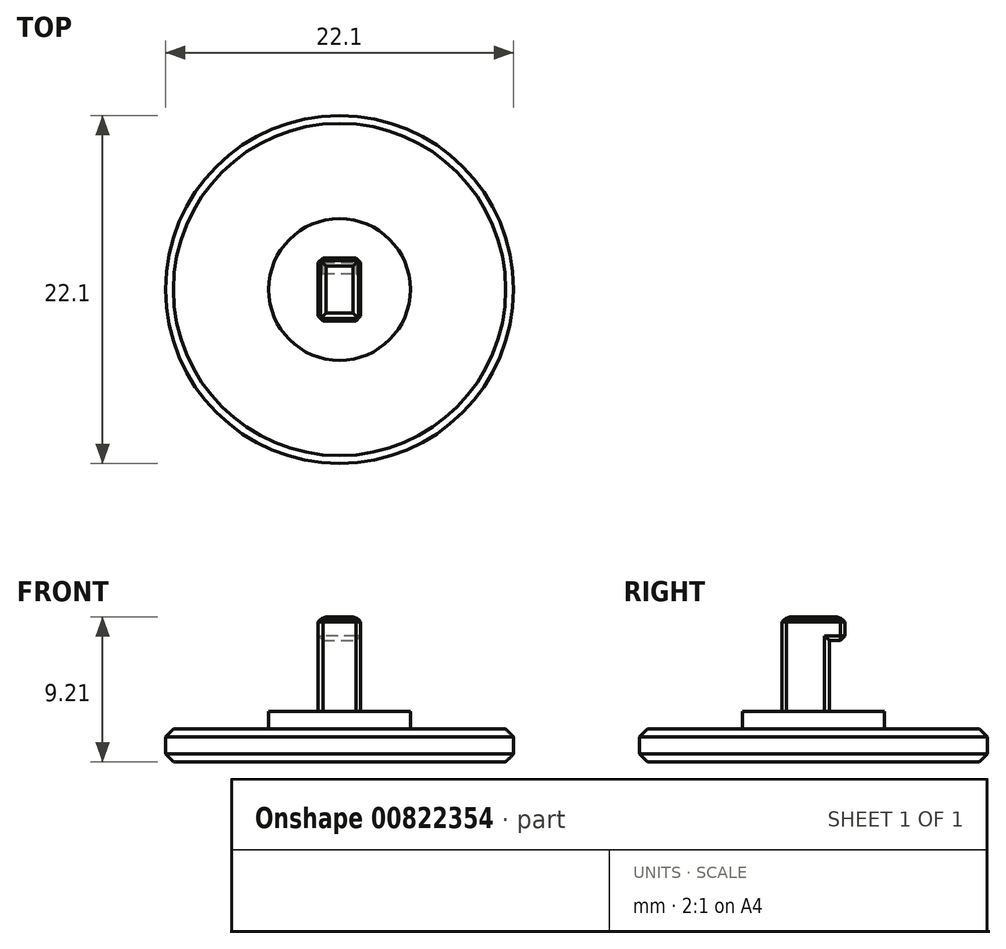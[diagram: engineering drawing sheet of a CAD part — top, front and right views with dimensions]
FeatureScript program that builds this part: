
annotation { "Feature Type Name" : "Feature", "Feature Type Description" : "" }
export const myFeature = defineFeature(function(context is Context, id is Id, definition is map)
    precondition{}
    {
        {
            var Q0;
            Q0=qCreatedBy(makeId("Top.planeOp"),FACE);
            var sketch = newSketch(context, id + "F0", { "sketchPlane" : qUnion([Q0])});
            skCircle(sketch, "E0", {"center": v(0, 0) * mm, "radius": 11.05 * mm});
            skSolve(sketch);
        }
        {
            var Q0;
            Q0=qSketchRegion(id+"F0",true);
            extrude(context, id + "F1", {"entities" : qUnion([Q0]), "depth" : 2.1 * mm, "offsetDistance" : 25 * mm});
        }
        {
            var Q0;
            Q0=makeQuery(id+"F1.opExtrude","CAP_FACE",FACE,{"disambiguationData":[OSD([sQuery(id+"F0.wireOp",EDGE,"E0")])],"isStart":false});
            var sketch = newSketch(context, id + "F2", { "sketchPlane" : qUnion([Q0])});
            skCircle(sketch, "E1", {"center": v(0, 0) * mm, "radius": 4.5 * mm});
            skSolve(sketch);
        }
        {
            var Q0;
            Q0=makeQuery(id+"F2.imprint","IMPRINT",FACE,{"disambiguationData":[TD([[makeQuery(id+"F2.imprint","IMPRINT",EDGE,{"derivedFrom":sQuery(id+"F2.wireOp",EDGE,"E1")}),1.0]])]});
            extrude(context, id + "F3", {"entities" : qUnion([Q0]), "operationType" : NewBodyOperationType.ADD, "depth" : 1.11 * mm, "offsetDistance" : 25 * mm});
        }
        {
            var Q0;
            Q0=makeQuery(id+"F3.opExtrude","CAP_FACE",FACE,{"disambiguationData":[OSD([sQuery(id+"F2.wireOp",EDGE,"E1")])],"isStart":false});
            var sketch = newSketch(context, id + "F4", { "sketchPlane" : qUnion([Q0])});
            skCircle(sketch, "E2", {"center": v(0, 0) * mm, "radius": 4 * mm});
            skSolve(sketch);
        }
        {
            var Q0;
            Q0=makeQuery(id+"F4.imprint","IMPRINT",FACE,{"disambiguationData":[TD([[makeQuery(id+"F4.imprint","IMPRINT",EDGE,{"derivedFrom":sQuery(id+"F4.wireOp",EDGE,"E2")}),1.0]])]});
            var sketch = newSketch(context, id + "F5", { "sketchPlane" : qUnion([Q0])});
            skLineSegment(sketch, "E3.top", {"start": v(1.35, -2) * mm, "end": v(-1.35, -2) * mm});
            skLineSegment(sketch, "E3.left", {"start": v(1.35, 1) * mm, "end": v(1.35, -2) * mm});
            skLineSegment(sketch, "E3.right", {"start": v(-1.35, 1) * mm, "end": v(-1.35, -2) * mm});
            skPoint(sketch, "E3.middle", {"position": v(0, 0) * mm});
            skLineSegment(sketch, "E4.bottom", {"start": v(-1.35, -2) * mm, "end": v(1.35, -2) * mm});
            skLineSegment(sketch, "E4.left", {"start": v(-1.35, -2) * mm, "end": v(-1.35, 0) * mm});
            skLineSegment(sketch, "E4.right", {"start": v(1.35, -2) * mm, "end": v(1.35, 0) * mm});
            skLineSegment(sketch, "E5.top", {"start": v(-1.35, 1) * mm, "end": v(1.35, 1) * mm});
            skLineSegment(sketch, "E5.left", {"start": v(-1.35, 0) * mm, "end": v(-1.35, 1) * mm});
            skLineSegment(sketch, "E5.right", {"start": v(1.35, 0) * mm, "end": v(1.35, 1) * mm});
            skPoint(sketch, "E6.orphan", {"position": v(-1.35, 2) * mm});
            skPoint(sketch, "E7.orphan", {"position": v(1.35, 2) * mm});
            skSolve(sketch);
        }
        {
            var Q0;
            {var subQ1=sQuery(id+"F5.wireOp",EDGE,"E3.top");Q0=makeQuery(id+"F5.imprint","IMPRINT",FACE,{"disambiguationData":[TD([[makeQuery(id+"F5.imprint","IMPRINT",EDGE,{"derivedFrom":subQ1}),-1.0]])]});}
            extrude(context, id + "F6", {"entities" : qUnion([Q0]), "operationType" : NewBodyOperationType.ADD, "depth" : 6 * mm, "offsetDistance" : 25 * mm});
        }
        {
            var Q0;
            Q0=makeQuery(id+"F6.opExtrude","SWEPT_FACE",FACE,{"disambiguationData":[OSD([sQuery(id+"F5.wireOp",EDGE,"E5.top")])]});
            var sketch = newSketch(context, id + "F7", { "sketchPlane" : qUnion([Q0])});
            skLineSegment(sketch, "E8.bottom", {"start": v(1.35, 9.2) * mm, "end": v(-1.35, 9.2) * mm});
            skLineSegment(sketch, "E8.top", {"start": v(1.35, 7.7) * mm, "end": v(-1.35, 7.7) * mm});
            skLineSegment(sketch, "E8.left", {"start": v(1.35, 9.2) * mm, "end": v(1.35, 7.7) * mm});
            skLineSegment(sketch, "E8.right", {"start": v(-1.35, 9.2) * mm, "end": v(-1.35, 7.7) * mm});
            skSolve(sketch);
        }
        {
            var Q0;
            Q0=makeQuery(id+"F7.imprint","IMPRINT",FACE,{"disambiguationData":[TD([[makeQuery(id+"F7.imprint","IMPRINT",EDGE,{"derivedFrom":sQuery(id+"F7.wireOp",EDGE,"E8.bottom")}),1.0]])]});
            extrude(context, id + "F8", {"entities" : qUnion([Q0]), "operationType" : NewBodyOperationType.ADD, "depth" : 1 * mm, "offsetDistance" : 25 * mm});
        }
        {
            var Q0;
            Q0=makeQuery(id+"F6.opExtrude","SWEPT_EDGE",EDGE,{"disambiguationData":[OSD([sQuery(id+"F5.wireOp",EDGE,"E3.top"),sQuery(id+"F5.wireOp",EDGE,"E3.right")])]});
            var Q1;
            Q1=makeQuery(id+"F6.opExtrude","SWEPT_EDGE",EDGE,{"disambiguationData":[OSD([sQuery(id+"F5.wireOp",EDGE,"E3.top"),sQuery(id+"F5.wireOp",EDGE,"E3.left")])]});
            var Q2;
            Q2=makeQuery(id+"F6.opExtrude","SWEPT_EDGE",EDGE,{"disambiguationData":[OSD([sQuery(id+"F5.wireOp",EDGE,"E3.left"),sQuery(id+"F5.wireOp",EDGE,"E5.top")])]});
            var Q3;
            Q3=makeQuery(id+"F6.opExtrude","SWEPT_EDGE",EDGE,{"disambiguationData":[OSD([sQuery(id+"F5.wireOp",EDGE,"E3.right"),sQuery(id+"F5.wireOp",EDGE,"E5.top")])]});
            var Q4;
            Q4=makeQuery(id+"F8.opExtrude","SWEPT_EDGE",EDGE,{"disambiguationData":[OSD([sQuery(id+"F5.wireOp",EDGE,"E3.left"),sQuery(id+"F5.wireOp",EDGE,"E5.top"),sQuery(id+"F7.wireOp",EDGE,"E8.top"),sQuery(id+"F7.wireOp",EDGE,"E8.right")])]});
            var Q5;
            Q5=makeQuery(id+"F8.opExtrude","SWEPT_EDGE",EDGE,{"disambiguationData":[OSD([sQuery(id+"F5.wireOp",EDGE,"E3.right"),sQuery(id+"F5.wireOp",EDGE,"E5.top"),sQuery(id+"F7.wireOp",EDGE,"E8.top"),sQuery(id+"F7.wireOp",EDGE,"E8.left")])]});
            var Q6;
            Q6=makeQuery(id+"F8.opExtrude","CAP_EDGE",EDGE,{"disambiguationData":[OSD([sQuery(id+"F7.wireOp",EDGE,"E8.top")])],"isStart":false});
            var Q7;
            Q7=makeQuery(id+"F8.opExtrude","CAP_EDGE",EDGE,{"disambiguationData":[OSD([sQuery(id+"F7.wireOp",EDGE,"E8.right")])],"isStart":false});
            var Q8;
            Q8=makeQuery(id+"F8.opExtrude","CAP_EDGE",EDGE,{"disambiguationData":[OSD([sQuery(id+"F7.wireOp",EDGE,"E8.left")])],"isStart":false});
            var Q9;
            Q9=makeQuery(id+"F8.opExtrude","CAP_EDGE",EDGE,{"disambiguationData":[OSD([sQuery(id+"F7.wireOp",EDGE,"E8.bottom")])],"isStart":false});
            var Q10;
            Q10=makeQuery(id+"F8.boolean.opBoolean","MERGE",EDGE,{"derivedFrom":[makeQuery(id+"F6.opExtrude","CAP_EDGE",EDGE,{"disambiguationData":[OSD([sQuery(id+"F5.wireOp",EDGE,"E3.left")])],"isStart":false}),makeQuery(id+"F8.opExtrude","SWEPT_EDGE",EDGE,{"disambiguationData":[OSD([sQuery(id+"F7.wireOp",EDGE,"E8.bottom"),sQuery(id+"F7.wireOp",EDGE,"E8.right")])]})]});
            var Q11;
            Q11=makeQuery(id+"F8.boolean.opBoolean","MERGE",EDGE,{"derivedFrom":[makeQuery(id+"F6.opExtrude","CAP_EDGE",EDGE,{"disambiguationData":[OSD([sQuery(id+"F5.wireOp",EDGE,"E3.right")])],"isStart":false}),makeQuery(id+"F8.opExtrude","SWEPT_EDGE",EDGE,{"disambiguationData":[OSD([sQuery(id+"F7.wireOp",EDGE,"E8.bottom"),sQuery(id+"F7.wireOp",EDGE,"E8.left")])]})]});
            var Q12;
            Q12=makeQuery(id+"F6.opExtrude","CAP_EDGE",EDGE,{"disambiguationData":[OSD([sQuery(id+"F5.wireOp",EDGE,"E3.top")])],"isStart":false});
            var Q13;
            Q13=makeQuery(id+"F6.opExtrude","CAP_EDGE",EDGE,{"disambiguationData":[OSD([sQuery(id+"F5.wireOp",EDGE,"E3.right")])],"isStart":true});
            chamfer(context, id + "F9", {"entities" : qUnion([Q0, Q1, Q2, Q3, Q4, Q5, Q6, Q7, Q8, Q9, Q10, Q11, Q12, Q13]), "width" : .3 * mm, "tangentPropagation" : true});
        }
        {
            var Q0;
            Q0=makeQuery(id+"F1.opExtrude","CAP_EDGE",EDGE,{"disambiguationData":[OSD([sQuery(id+"F0.wireOp",EDGE,"E0")])],"isStart":true});
            var Q1;
            Q1=makeQuery(id+"F1.opExtrude","CAP_EDGE",EDGE,{"disambiguationData":[OSD([sQuery(id+"F0.wireOp",EDGE,"E0")])],"isStart":false});
            chamfer(context, id + "F10", {"entities" : qUnion([Q0, Q1]), "width" : .5 * mm, "tangentPropagation" : true});
        }
        {
            var Q0;
            Q0=makeQuery(id+"F6.opExtrude","SWEPT_EDGE",EDGE,{"disambiguationData":[OSD([sQuery(id+"F5.wireOp",EDGE,"E4.bottom"),sQuery(id+"F5.wireOp",EDGE,"E4.right")])]});
            var Q1;
            Q1=makeQuery(id+"F6.opExtrude","SWEPT_EDGE",EDGE,{"disambiguationData":[OSD([sQuery(id+"F5.wireOp",EDGE,"E5.top"),sQuery(id+"F5.wireOp",EDGE,"E5.right")])]});
            var Q2;
            Q2=makeQuery(id+"F6.opExtrude","SWEPT_EDGE",EDGE,{"disambiguationData":[OSD([sQuery(id+"F5.wireOp",EDGE,"E5.top"),sQuery(id+"F5.wireOp",EDGE,"E5.left")])]});
            var Q3;
            Q3=makeQuery(id+"F8.opExtrude","CAP_EDGE",EDGE,{"disambiguationData":[OSD([sQuery(id+"F7.wireOp",EDGE,"E8.top")])],"isStart":true});
            var Q4;
            Q4=makeQuery(id+"F8.opExtrude","CAP_EDGE",EDGE,{"disambiguationData":[OSD([sQuery(id+"F7.wireOp",EDGE,"E8.right")])],"isStart":false});
            var Q5;
            Q5=makeQuery(id+"F8.boolean.opBoolean","MERGE",FACE,{"derivedFrom":[makeQuery(id+"F6.opExtrude","CAP_FACE",FACE,{"disambiguationData":[OSD([sQuery(id+"F5.wireOp",EDGE,"E3.top"),sQuery(id+"F5.wireOp",EDGE,"E3.left"),sQuery(id+"F5.wireOp",EDGE,"E3.right"),sQuery(id+"F5.wireOp",EDGE,"E5.top")])],"isStart":false}),makeQuery(id+"F8.opExtrude","SWEPT_FACE",FACE,{"disambiguationData":[OSD([sQuery(id+"F7.wireOp",EDGE,"E8.bottom")])]})]});
            var Q6;
            Q6=makeQuery(id+"F6.opExtrude","SWEPT_EDGE",EDGE,{"disambiguationData":[OSD([sQuery(id+"F5.wireOp",EDGE,"E4.bottom"),sQuery(id+"F5.wireOp",EDGE,"E4.left")])]});
            var Q7;
            Q7=makeQuery(id+"F8.opExtrude","SWEPT_EDGE",EDGE,{"disambiguationData":[OSD([sQuery(id+"F5.wireOp",EDGE,"E5.top"),sQuery(id+"F5.wireOp",EDGE,"E5.left"),sQuery(id+"F7.wireOp",EDGE,"E8.top"),sQuery(id+"F7.wireOp",EDGE,"E8.left")])]});
            var Q8;
            Q8=makeQuery(id+"F8.opExtrude","CAP_EDGE",EDGE,{"disambiguationData":[OSD([sQuery(id+"F7.wireOp",EDGE,"E8.left")])],"isStart":false});
            var Q9;
            Q9=makeQuery(id+"F8.opExtrude","SWEPT_EDGE",EDGE,{"disambiguationData":[OSD([sQuery(id+"F5.wireOp",EDGE,"E5.top"),sQuery(id+"F5.wireOp",EDGE,"E5.right"),sQuery(id+"F7.wireOp",EDGE,"E8.top"),sQuery(id+"F7.wireOp",EDGE,"E8.right")])]});
            var Q10;
            Q10=makeQuery(id+"F8.opExtrude","CAP_EDGE",EDGE,{"disambiguationData":[OSD([sQuery(id+"F7.wireOp",EDGE,"E8.top")])],"isStart":false});
            chamfer(context, id + "F11", {"entities" : qUnion([Q0, Q1, Q2, Q3, Q4, Q5, Q6, Q7, Q8, Q9, Q10]), "width" : 0.5 * mm, "tangentPropagation" : true});
        }
    });
